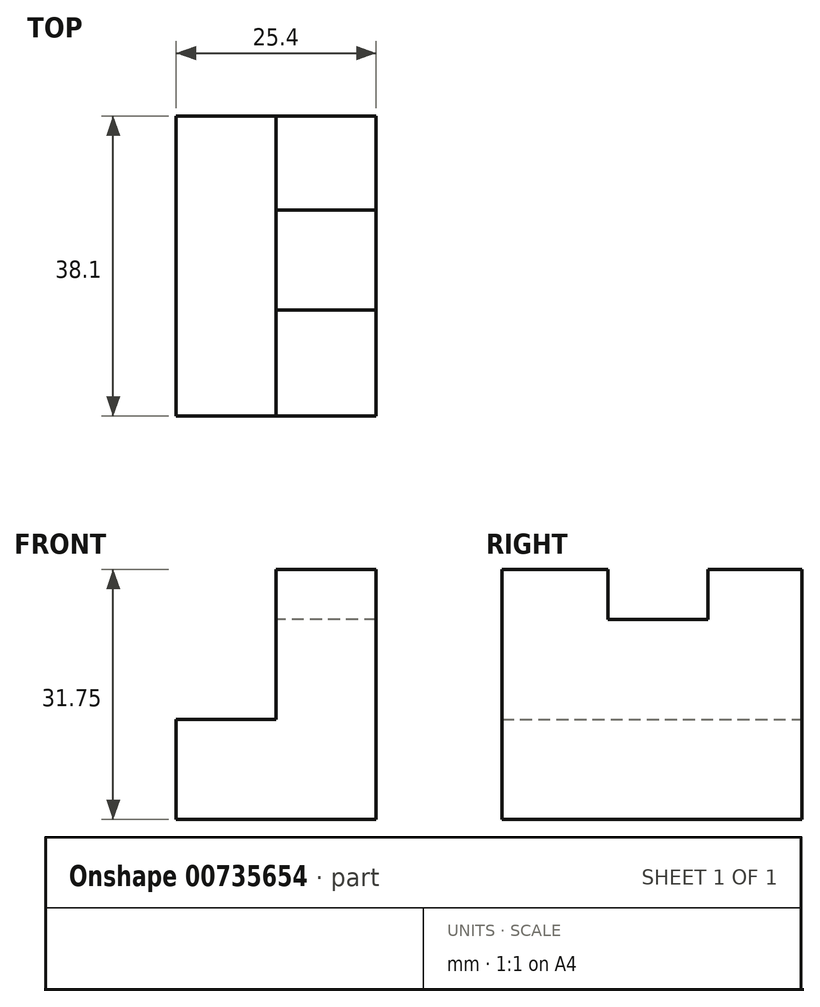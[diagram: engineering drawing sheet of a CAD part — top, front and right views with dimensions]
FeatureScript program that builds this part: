
annotation { "Feature Type Name" : "Feature", "Feature Type Description" : "" }
export const myFeature = defineFeature(function(context is Context, id is Id, definition is map)
    precondition{}
    {
        {
            var Q0;
            Q0=qCreatedBy(makeId("Front.planeOp"),FACE);
            var sketch = newSketch(context, id + "F0", { "sketchPlane" : qUnion([Q0])});
            skLineSegment(sketch, "E0", {"start": v(0, 0) * mm, "end": v(25.4, 0) * mm});
            skLineSegment(sketch, "E1", {"start": v(25.4, 0) * mm, "end": v(25.4, 31.75) * mm});
            skLineSegment(sketch, "E2", {"start": v(25.4, 31.75) * mm, "end": v(12.7, 31.75) * mm});
            skLineSegment(sketch, "E3", {"start": v(0, 0) * mm, "end": v(0, 12.7) * mm});
            skLineSegment(sketch, "E4", {"start": v(0, 12.7) * mm, "end": v(12.7, 12.7) * mm});
            skLineSegment(sketch, "E5", {"start": v(12.7, 12.7) * mm, "end": v(12.7, 31.75) * mm});
            skSolve(sketch);
        }
        {
            var Q0;
            Q0=makeQuery(id+"F0.imprint","IMPRINT",FACE,{"disambiguationData":[TD([[makeQuery(id+"F0.imprint","IMPRINT",EDGE,{"derivedFrom":sQuery(id+"F0.wireOp",EDGE,"E0")}),1.0]])]});
            extrude(context, id + "F1", {"entities" : qUnion([Q0]), "depth" : 38.1 * mm, "offsetDistance" : 25.4 * mm});
        }
        {
            var Q0;
            Q0=makeQuery(id+"F1.opExtrude","SWEPT_FACE",FACE,{"disambiguationData":[OSD([sQuery(id+"F0.wireOp",EDGE,"E5")])]});
            var sketch = newSketch(context, id + "F2", { "sketchPlane" : qUnion([Q0])});
            skLineSegment(sketch, "E6", {"start": v(11.97, 31.75) * mm, "end": v(11.97, 25.4) * mm});
            skLineSegment(sketch, "E7", {"start": v(11.97, 25.4) * mm, "end": v(24.67, 25.4) * mm});
            skLineSegment(sketch, "E8", {"start": v(24.67, 25.4) * mm, "end": v(24.67, 31.75) * mm});
            skLineSegment(sketch, "E9", {"start": v(11.97, 31.75) * mm, "end": v(24.67, 31.75) * mm});
            skSolve(sketch);
        }
        {
            var Q0;
            Q0=makeQuery(id+"F2.imprint","IMPRINT",FACE,{"disambiguationData":[TD([[makeQuery(id+"F2.imprint","IMPRINT",EDGE,{"derivedFrom":sQuery(id+"F2.wireOp",EDGE,"E6")}),1.0]])]});
            extrude(context, id + "F3", {"entities" : qUnion([Q0]), "operationType" : NewBodyOperationType.REMOVE, "oppositeDirection" : true, "depth" : 12.7 * mm, "offsetDistance" : 25.4 * mm});
        }
    });
